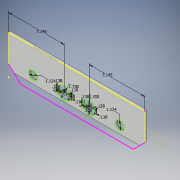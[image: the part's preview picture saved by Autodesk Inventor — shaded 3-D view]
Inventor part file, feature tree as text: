
AUTODESK INVENTOR PART (.ipt)
format: ipt  version: 2017 (Build 210142000, 142)  size: 173,568 bytes
history: native  units: in
note: dims shown in document units (in); Inventor stores cm internally (conversion verified against a paired STEP export)
features: extrude x5, sketch x3, projected_geometry x3, thicken_offset x1
ambient origin geometry x8: Origin, YZ Plane, XZ Plane, XY Plane, X Axis, Y Axis, Z Axis, Center Point
bodies: Solid1 (feature_tree)
feature tree (12):
  extrude  "Extrusion1"  Depth=5.0in
  extrude  "Extrusion2"  Depth=0.25in TaperAngle=0.0deg
  sketch  "Sketch3"  dims[d10=1.124in d14=2.0in d15=0.0in d18=1.124in d19=1.5in d20=180.0deg d31=1.7in d32=1.7in d33=1.0in d34=0.0in d53=0.82in d54=0.82in d55=0.945in d56=0.276in d57=0.138in d58=0.276in d59=0.138in d60=0.945in d61=0.276in d62=0.276in d63=0.138in d64=0.138in d65=0.945in d66=0.945in d67=0.138in d68=0.138in d69=0.138in d70=0.138in d71=1.0in d72=0.0in d73=0.25in d74=7.145in d75=7.145in]
  extrude  "Extrusion3"  Depth=0.25in TaperAngle=0.0deg
  extrude  "Extrusion4"  Depth=0.25in
  thicken_offset  "Thicken1"
  extrude  "Extrusion6"  Depth=0.25in
  sketch  "Sketch1"  dims[d0=17.5in d1=5.0in]
  sketch  "Sketch2"  dims[d2=0.25in d3=0.0in d4=2.0in d5=0.0in]
  projected_geometry  "Projected Loop1"
  projected_geometry  "Projected Loop2"
  projected_geometry  "Project Cut Edges1"
